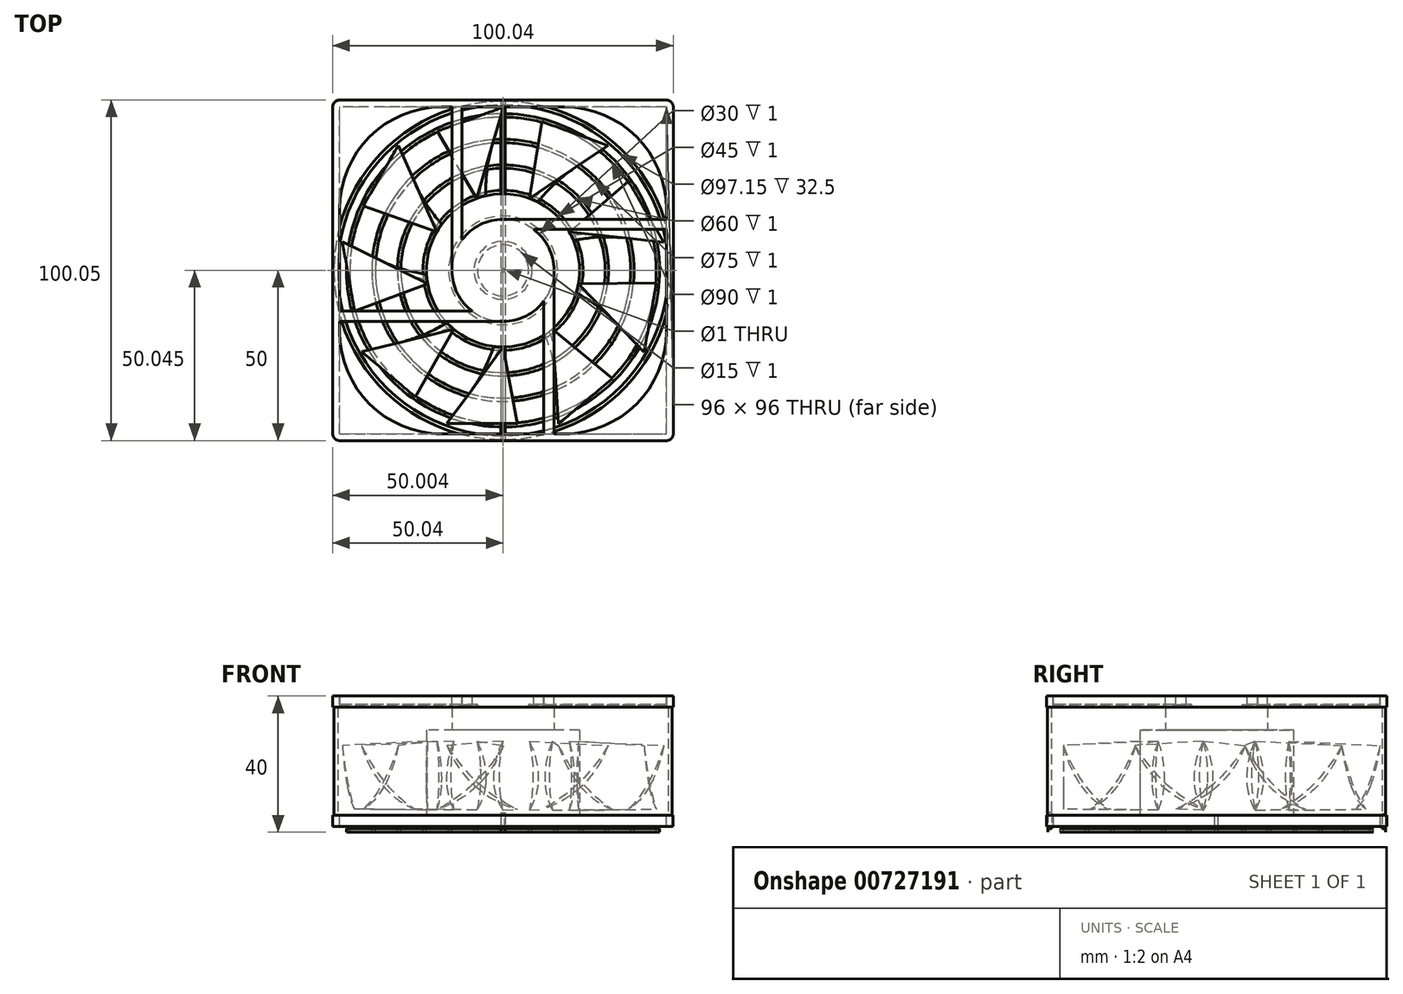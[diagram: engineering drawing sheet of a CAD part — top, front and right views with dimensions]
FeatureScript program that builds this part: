
annotation { "Feature Type Name" : "Feature", "Feature Type Description" : "" }
export const myFeature = defineFeature(function(context is Context, id is Id, definition is map)
    precondition{}
    {
        {
            var Q0;
            Q0=qCreatedBy(makeId("Top.planeOp"),FACE);
            var sketch = newSketch(context, id + "F0", { "sketchPlane" : qUnion([Q0])});
            skCircle(sketch, "E0", {"center": v(0, 0) * mm, "radius": 22.5 * mm});
            skSolve(sketch);
        }
        {
            var Q0;
            Q0=makeQuery(id+"F0.imprint","IMPRINT",FACE,{"disambiguationData":[TD([[makeQuery(id+"F0.imprint","IMPRINT",EDGE,{"derivedFrom":sQuery(id+"F0.wireOp",EDGE,"E0")}),1.0]])]});
            extrude(context, id + "F1", {"entities" : qUnion([Q0]), "depth" : 25 * mm, "offsetDistance" : 25 * mm});
        }
        {
            var Q0;
            Q0=qCreatedBy(makeId("Front.planeOp"),FACE);
            cPlane(context, id + "F2", {"entities" : qUnion([Q0]), "cplaneType" : CPlaneType.OFFSET, "offset" : 22.5 * mm, "width" : 150 * mm, "height" : 150 * mm});
        }
        {
            var Q0;
            Q0=qCreatedBy(id+"F2.planeOp",FACE);
            var sketch = newSketch(context, id + "F3", { "sketchPlane" : qUnion([Q0])});
            skArc(sketch, "E1", {"start": v(0, 21.74) * mm, "mid": v(-2.32, 15.5) * mm, "end": v(-2.7, 8.85) * mm});
            skArc(sketch, "E2", {"start": v(0, 21.74) * mm, "mid": v(-1.2, 11.6) * mm, "end": v(0, 1.47) * mm});
            skArc(sketch, "E3", {"start": v(-2.56, 14.16) * mm, "mid": v(-2.5, 7.57) * mm, "end": v(0, 1.47) * mm});
            skSolve(sketch);
        }
        {
            var Q0;
            Q0=qCreatedBy(id+"F2.planeOp",FACE);
            cPlane(context, id + "F4", {"entities" : qUnion([Q0]), "cplaneType" : CPlaneType.OFFSET, "offset" : 22.5 * mm, "width" : 150 * mm, "height" : 150 * mm});
        }
        {
            var Q0;
            Q0=qCreatedBy(id+"F4.planeOp",FACE);
            var sketch = newSketch(context, id + "F5", { "sketchPlane" : qUnion([Q0])});
            skArc(sketch, "E4", {"start": v(-16.45, 20.45) * mm, "mid": v(-8.34, 8.67) * mm, "end": v(4.18, 1.74) * mm});
            skArc(sketch, "E5", {"start": v(-16.45, 20.45) * mm, "mid": v(-7.5, 9.6) * mm, "end": v(4.18, 1.74) * mm});
            skSolve(sketch);
        }
        {
            var Q0;
            Q0=makeQuery(id+"F3.imprint","IMPRINT",FACE,{"disambiguationData":[TD([[makeQuery(id+"F3.imprint","IMPRINT",EDGE,{"derivedFrom":sQuery(id+"F3.wireOp",EDGE,"E1")}),1.0]])]});
            var Q1;
            Q1=makeQuery(id+"F5.imprint","IMPRINT",FACE,{"disambiguationData":[TD([[makeQuery(id+"F5.imprint","IMPRINT",EDGE,{"derivedFrom":sQuery(id+"F5.wireOp",EDGE,"E4")}),1.0]])]});
            loft(context, id + "F6", {"sheetProfilesArray" : [{ "sheetProfileEntities" : qUnion([Q0]) }, { "sheetProfileEntities" : qUnion([Q1]) }]});
        }
        {
            var Q0;
            {var subQ0=sQuery(id+"F3.wireOp",EDGE,"E2");Q0=makeQuery(id+"F6.opLoft","SWEPT_BODY",BODY,{"disambiguationData":[OSD([makeQuery(id+"F3.imprint","IMPRINT",FACE,{"disambiguationData":[TD([[makeQuery(id+"F3.imprint","IMPRINT",EDGE,{"derivedFrom":subQ0}),-1.0]])]}),makeQuery(id+"F5.imprint","IMPRINT",FACE,{"disambiguationData":[TD([[makeQuery(id+"F5.imprint","IMPRINT",EDGE,{"derivedFrom":sQuery(id+"F5.wireOp",EDGE,"E4")}),1.0]])]})])]});}
            var Q1;
            Q1=makeQuery(id+"F1.opExtrude","SWEPT_FACE",FACE,{"disambiguationData":[OSD([sQuery(id+"F0.wireOp",EDGE,"E0")])]});
            circularPattern(context, id + "F7", {"entities" : qUnion([Q0]), "axis" : qUnion([Q1]), "angle" : 360 * degree, "instanceCount" : 9, "equalSpace" : true});
        }
        {
            var Q0;
            Q0=makeQuery(id+"F1.opExtrude","CAP_FACE",FACE,{"disambiguationData":[OSD([sQuery(id+"F0.wireOp",EDGE,"E0")])],"isStart":false});
            var sketch = newSketch(context, id + "F8", { "sketchPlane" : qUnion([Q0])});
            skCircle(sketch, "E6", {"center": v(0, 0) * mm, "radius": 15 * mm});
            skSolve(sketch);
        }
        {
            var Q0;
            Q0 = qSketchRegion(id + "F8", true);
            extrude(context, id + "F9", {"entities" : qUnion([Q0]), "operationType" : NewBodyOperationType.ADD, "depth" : 10 * mm, "offsetDistance" : 25 * mm});
        }
        {
            var Q0;
            Q0=makeQuery(id+"F9.opExtrude","CAP_FACE",FACE,{"disambiguationData":[OSD([sQuery(id+"F8.wireOp",EDGE,"E6")])],"isStart":false});
            var sketch = newSketch(context, id + "F10", { "sketchPlane" : qUnion([Q0])});
            skLineSegment(sketch, "E7", {"start": v(-15, 0) * mm, "end": v(-15, 50) * mm});
            skLineSegment(sketch, "E8", {"start": v(0, 15) * mm, "end": v(50, 15) * mm});
            skLineSegment(sketch, "E9", {"start": v(15, 0) * mm, "end": v(15, -50) * mm});
            skLineSegment(sketch, "E10", {"start": v(0, -15) * mm, "end": v(-50, -15) * mm});
            skLineSegment(sketch, "E11", {"start": v(-15, 50) * mm, "end": v(-12, 50) * mm});
            skLineSegment(sketch, "E12", {"start": v(-12, 50) * mm, "end": v(-12, 9) * mm});
            skLineSegment(sketch, "E13", {"start": v(50, 15) * mm, "end": v(50, 12) * mm});
            skLineSegment(sketch, "E14", {"start": v(15, -50) * mm, "end": v(12, -50) * mm});
            skLineSegment(sketch, "E15", {"start": v(-50, -15) * mm, "end": v(-50, -12) * mm});
            skLineSegment(sketch, "E16", {"start": v(-50, -12) * mm, "end": v(-9, -12) * mm});
            skLineSegment(sketch, "E17", {"start": v(12, -50) * mm, "end": v(12, -9) * mm});
            skLineSegment(sketch, "E18", {"start": v(50, 12) * mm, "end": v(9, 12) * mm});
            skCircle(sketch, "E19", {"center": v(0, 0) * mm, "radius": 15 * mm});
            skSolve(sketch);
        }
        {
            var Q0;
            Q0 = qSketchRegion(id + "F10", true);
            extrude(context, id + "F11", {"entities" : qUnion([Q0]), "operationType" : NewBodyOperationType.ADD, "oppositeDirection" : true, "depth" : 3.3 * mm, "offsetDistance" : 25 * mm});
        }
        {
            var Q0;
            Q0=makeQuery(id+"F11.boolean.opBoolean","MERGE",FACE,{"derivedFrom":[makeQuery(id+"F9.opExtrude","CAP_FACE",FACE,{"disambiguationData":[OSD([sQuery(id+"F8.wireOp",EDGE,"E6")])],"isStart":false}),makeQuery(id+"F11.opExtrude","CAP_FACE",FACE,{"disambiguationData":[OSD([sQuery(id+"F10.wireOp",EDGE,"E7"),sQuery(id+"F10.wireOp",EDGE,"E8"),sQuery(id+"F10.wireOp",EDGE,"E9"),sQuery(id+"F10.wireOp",EDGE,"E10"),sQuery(id+"F10.wireOp",EDGE,"E11"),sQuery(id+"F10.wireOp",EDGE,"E12"),sQuery(id+"F10.wireOp",EDGE,"E13"),sQuery(id+"F10.wireOp",EDGE,"E14"),sQuery(id+"F10.wireOp",EDGE,"E15"),sQuery(id+"F10.wireOp",EDGE,"E16"),sQuery(id+"F10.wireOp",EDGE,"E17"),sQuery(id+"F10.wireOp",EDGE,"E18"),sQuery(id+"F10.wireOp",EDGE,"E19")])],"isStart":true})]});
            var sketch = newSketch(context, id + "F12", { "sketchPlane" : qUnion([Q0])});
            skLineSegment(sketch, "E20", {"start": v(-12, 50) * mm, "end": v(50, 50) * mm});
            skLineSegment(sketch, "E21", {"start": v(50, 50) * mm, "end": v(50, -50) * mm});
            skLineSegment(sketch, "E22", {"start": v(48, -50) * mm, "end": v(-50, -50) * mm});
            skLineSegment(sketch, "E23", {"start": v(-50, -50) * mm, "end": v(-50, 50) * mm});
            skLineSegment(sketch, "E24", {"start": v(-50, 50) * mm, "end": v(-12, 50) * mm});
            skLineSegment(sketch, "E25", {"start": v(-48, -48) * mm, "end": v(-48, 48) * mm});
            skLineSegment(sketch, "E26", {"start": v(48, 48) * mm, "end": v(-48, 48) * mm});
            skLineSegment(sketch, "E27", {"start": v(-48, -48) * mm, "end": v(48, -48) * mm});
            skLineSegment(sketch, "E28", {"start": v(48, -48) * mm, "end": v(48, 48) * mm});
            skPoint(sketch, "E29.end.orphan", {"position": v(48, -50) * mm});
            skLineSegment(sketch, "E30", {"start": v(48, -50) * mm, "end": v(50, -50) * mm});
            skSolve(sketch);
        }
        {
            var Q0;
            Q0 = qSketchRegion(id + "F12", true);
            extrude(context, id + "F13", {"entities" : qUnion([Q0]), "operationType" : NewBodyOperationType.ADD, "oppositeDirection" : true, "depth" : 3.3 * mm, "offsetDistance" : 25 * mm});
        }
        {
            var Q0;
            Q0=makeQuery(id+"F1.opExtrude","CAP_FACE",FACE,{"disambiguationData":[OSD([sQuery(id+"F0.wireOp",EDGE,"E0")])],"isStart":true});
            var sketch = newSketch(context, id + "F14", { "sketchPlane" : qUnion([Q0])});
            skCircle(sketch, "E31", {"center": v(0, 0) * mm, "radius": 48.58 * mm});
            skCircle(sketch, "E32", {"center": v(0, 0) * mm, "radius": 49.67 * mm});
            skSolve(sketch);
        }
        {
            var Q0;
            Q0=makeQuery(id+"F14.imprint","IMPRINT",FACE,{"disambiguationData":[TD([[makeQuery(id+"F14.imprint","IMPRINT",EDGE,{"derivedFrom":sQuery(id+"F14.wireOp",EDGE,"E31")}),-1.0]])]});
            extrude(context, id + "F15", {"entities" : qUnion([Q0]), "operationType" : NewBodyOperationType.ADD, "oppositeDirection" : true, "depth" : 32.5 * mm, "offsetDistance" : 25 * mm});
        }
        {
            var Q0;
            Q0=makeQuery(id+"F13.opExtrude","SWEPT_EDGE",EDGE,{"disambiguationData":[OSD([sQuery(id+"F12.wireOp",EDGE,"E22"),sQuery(id+"F12.wireOp",EDGE,"E23")])]});
            fillet(context, id + "F16", {"entities" : qUnion([Q0]), "radius" : 2 * mm, "tangentPropagation" : true, "allowEdgeOverflow" : false});
        }
        {
            var Q0;
            Q0=makeQuery(id+"F13.opExtrude","SWEPT_EDGE",EDGE,{"disambiguationData":[OSD([sQuery(id+"F12.wireOp",EDGE,"E20"),sQuery(id+"F12.wireOp",EDGE,"E21")])]});
            var Q1;
            Q1=makeQuery(id+"F13.opExtrude","SWEPT_EDGE",EDGE,{"disambiguationData":[OSD([sQuery(id+"F12.wireOp",EDGE,"E23"),sQuery(id+"F12.wireOp",EDGE,"E24")])]});
            var Q2;
            Q2=makeQuery(id+"F13.opExtrude","SWEPT_EDGE",EDGE,{"disambiguationData":[OSD([sQuery(id+"F12.wireOp",EDGE,"E21"),sQuery(id+"F12.wireOp",EDGE,"E30")])]});
            fillet(context, id + "F17", {"entities" : qUnion([Q0, Q1, Q2]), "radius" : 2 * mm, "tangentPropagation" : true, "allowEdgeOverflow" : false});
        }
        {
            var Q0;
            Q0=makeQuery(id+"F1.opExtrude","CAP_FACE",FACE,{"disambiguationData":[OSD([sQuery(id+"F0.wireOp",EDGE,"E0")])],"isStart":true});
            var sketch = newSketch(context, id + "F18", { "sketchPlane" : qUnion([Q0])});
            skCircle(sketch, "E33", {"center": v(0, 0) * mm, "radius": 0.5 * mm});
            skSolve(sketch);
        }
        {
            var Q0;
            Q0=makeQuery(id+"F18.imprint","IMPRINT",FACE,{"disambiguationData":[TD([[makeQuery(id+"F18.imprint","IMPRINT",EDGE,{"derivedFrom":sQuery(id+"F18.wireOp",EDGE,"E33")}),1.0]])]});
            extrude(context, id + "F19", {"entities" : qUnion([Q0]), "operationType" : NewBodyOperationType.ADD, "depth" : 4 * mm, "offsetDistance" : 25 * mm});
        }
        {
            var Q0;
            Q0=makeQuery(id+"F19.opExtrude","CAP_FACE",FACE,{"disambiguationData":[OSD([sQuery(id+"F18.wireOp",EDGE,"E33")])],"isStart":false});
            var sketch = newSketch(context, id + "F20", { "sketchPlane" : qUnion([Q0])});
            skCircle(sketch, "E34", {"center": v(0, 0) * mm, "radius": 7.5 * mm});
            skCircle(sketch, "E35", {"center": v(0, 0) * mm, "radius": 8.5 * mm});
            skCircle(sketch, "E36", {"center": v(0, 0) * mm, "radius": 15 * mm});
            skCircle(sketch, "E37", {"center": v(0, 0) * mm, "radius": 16 * mm});
            skCircle(sketch, "E38", {"center": v(0, 0) * mm, "radius": 22.5 * mm});
            skCircle(sketch, "E39", {"center": v(0, 0) * mm, "radius": 23.5 * mm});
            skCircle(sketch, "E40", {"center": v(0, 0) * mm, "radius": 30 * mm});
            skCircle(sketch, "E41", {"center": v(0, 0) * mm, "radius": 31 * mm});
            skCircle(sketch, "E42", {"center": v(0, 0) * mm, "radius": 37.5 * mm});
            skCircle(sketch, "E43", {"center": v(0, 0) * mm, "radius": 38.5 * mm});
            skCircle(sketch, "E44", {"center": v(0, 0) * mm, "radius": 45 * mm});
            skCircle(sketch, "E45", {"center": v(0, 0) * mm, "radius": 46 * mm});
            skSolve(sketch);
        }
        {
            var Q0;
            Q0=makeQuery(id+"F20.imprint","IMPRINT",FACE,{"disambiguationData":[TD([[makeQuery(id+"F20.imprint","IMPRINT",EDGE,{"derivedFrom":sQuery(id+"F20.wireOp",EDGE,"E34")}),-1.0]])]});
            var Q1;
            Q1=makeQuery(id+"F20.imprint","IMPRINT",FACE,{"disambiguationData":[TD([[makeQuery(id+"F20.imprint","IMPRINT",EDGE,{"derivedFrom":sQuery(id+"F20.wireOp",EDGE,"E36")}),-1.0]])]});
            var Q2;
            Q2=makeQuery(id+"F20.imprint","IMPRINT",FACE,{"disambiguationData":[TD([[makeQuery(id+"F20.imprint","IMPRINT",EDGE,{"derivedFrom":sQuery(id+"F20.wireOp",EDGE,"E38")}),-1.0]])]});
            var Q3;
            Q3=makeQuery(id+"F20.imprint","IMPRINT",FACE,{"disambiguationData":[TD([[makeQuery(id+"F20.imprint","IMPRINT",EDGE,{"derivedFrom":sQuery(id+"F20.wireOp",EDGE,"E40")}),-1.0]])]});
            var Q4;
            Q4=makeQuery(id+"F20.imprint","IMPRINT",FACE,{"disambiguationData":[TD([[makeQuery(id+"F20.imprint","IMPRINT",EDGE,{"derivedFrom":sQuery(id+"F20.wireOp",EDGE,"E42")}),-1.0]])]});
            var Q5;
            Q5=makeQuery(id+"F20.imprint","IMPRINT",FACE,{"disambiguationData":[TD([[makeQuery(id+"F20.imprint","IMPRINT",EDGE,{"derivedFrom":sQuery(id+"F20.wireOp",EDGE,"E44")}),-1.0]])]});
            extrude(context, id + "F21", {"entities" : qUnion([Q0, Q1, Q2, Q3, Q4, Q5]), "depth" : 1 * mm, "offsetDistance" : 25 * mm});
        }
        {
            var Q0;
            Q0=makeQuery(id+"F19.opExtrude","CAP_FACE",FACE,{"disambiguationData":[OSD([sQuery(id+"F18.wireOp",EDGE,"E33")])],"isStart":false});
            var sketch = newSketch(context, id + "F22", { "sketchPlane" : qUnion([Q0])});
            skLineSegment(sketch, "E46.bottom", {"start": v(-0.66, -49.64) * mm, "end": v(0.66, -49.64) * mm});
            skLineSegment(sketch, "E46.top", {"start": v(-0.66, 49.64) * mm, "end": v(0.66, 49.64) * mm});
            skLineSegment(sketch, "E46.left", {"start": v(-0.66, -49.64) * mm, "end": v(-0.66, 49.64) * mm});
            skLineSegment(sketch, "E46.right", {"start": v(0.66, -49.64) * mm, "end": v(0.66, 49.64) * mm});
            skPoint(sketch, "E46.middle", {"position": v(0, 0) * mm});
            skSolve(sketch);
        }
        {
            var Q0;
            Q0=makeQuery(id+"F22.imprint","IMPRINT",FACE,{"disambiguationData":[TD([[makeQuery(id+"F22.imprint","IMPRINT",EDGE,{"derivedFrom":sQuery(id+"F22.wireOp",EDGE,"E46.bottom")}),1.0]])]});
            extrude(context, id + "F23", {"entities" : qUnion([Q0]), "depth" : 1 * mm, "offsetDistance" : 25 * mm});
        }
        {
            var Q0;
            Q0=makeQuery(id+"F23.opExtrude","CAP_FACE",FACE,{"disambiguationData":[OSD([sQuery(id+"F18.wireOp",EDGE,"E33"),sQuery(id+"F22.wireOp",EDGE,"E46.bottom"),sQuery(id+"F22.wireOp",EDGE,"E46.top"),sQuery(id+"F22.wireOp",EDGE,"E46.left"),sQuery(id+"F22.wireOp",EDGE,"E46.right")])],"isStart":true});
            var sketch = newSketch(context, id + "F24", { "sketchPlane" : qUnion([Q0])});
            skLineSegment(sketch, "E47.bottom", {"start": v(0.66, 49.64) * mm, "end": v(-0.66, 49.64) * mm});
            skLineSegment(sketch, "E47.top", {"start": v(0.66, 48.64) * mm, "end": v(-0.66, 48.64) * mm});
            skLineSegment(sketch, "E47.left", {"start": v(0.66, 49.64) * mm, "end": v(0.66, 48.64) * mm});
            skLineSegment(sketch, "E47.right", {"start": v(-0.66, 49.64) * mm, "end": v(-0.66, 48.64) * mm});
            skSolve(sketch);
        }
        {
            var Q0;
            Q0=makeQuery(id+"F24.imprint","IMPRINT",FACE,{"disambiguationData":[TD([[makeQuery(id+"F24.imprint","IMPRINT",EDGE,{"derivedFrom":sQuery(id+"F24.wireOp",EDGE,"E47.bottom")}),-1.0]])]});
            extrude(context, id + "F25", {"entities" : qUnion([Q0]), "depth" : 4.35 * mm, "offsetDistance" : 25 * mm});
        }
        {
            var Q0;
            Q0=makeQuery(id+"F23.opExtrude","CAP_FACE",FACE,{"disambiguationData":[OSD([sQuery(id+"F18.wireOp",EDGE,"E33"),sQuery(id+"F22.wireOp",EDGE,"E46.bottom"),sQuery(id+"F22.wireOp",EDGE,"E46.top"),sQuery(id+"F22.wireOp",EDGE,"E46.left"),sQuery(id+"F22.wireOp",EDGE,"E46.right")])],"isStart":true});
            var sketch = newSketch(context, id + "F26", { "sketchPlane" : qUnion([Q0])});
            skLineSegment(sketch, "E48.bottom", {"start": v(-0.66, -49.64) * mm, "end": v(0.66, -49.64) * mm});
            skLineSegment(sketch, "E48.top", {"start": v(-0.66, -48.46) * mm, "end": v(0.66, -48.46) * mm});
            skLineSegment(sketch, "E48.left", {"start": v(-0.66, -49.64) * mm, "end": v(-0.66, -48.46) * mm});
            skLineSegment(sketch, "E48.right", {"start": v(0.66, -49.64) * mm, "end": v(0.66, -48.46) * mm});
            skSolve(sketch);
        }
        {
            var Q0;
            Q0=makeQuery(id+"F26.imprint","IMPRINT",FACE,{"disambiguationData":[TD([[makeQuery(id+"F26.imprint","IMPRINT",EDGE,{"derivedFrom":sQuery(id+"F26.wireOp",EDGE,"E48.bottom")}),1.0]])]});
            extrude(context, id + "F27", {"entities" : qUnion([Q0]), "depth" : 4.8 * mm, "offsetDistance" : 25 * mm});
        }
        {
            var Q0;
            Q0=qCreatedBy(makeId("Top.planeOp"),FACE);
            var sketch = newSketch(context, id + "F28", { "sketchPlane" : qUnion([Q0])});
            skLineSegment(sketch, "E49", {"start": v(-12.04, 50.05) * mm, "end": v(49.96, 50.05) * mm});
            skLineSegment(sketch, "E50", {"start": v(49.96, 50.05) * mm, "end": v(49.96, -49.95) * mm});
            skLineSegment(sketch, "E51", {"start": v(47.96, -49.95) * mm, "end": v(-50.04, -49.95) * mm});
            skLineSegment(sketch, "E52", {"start": v(-50.04, -49.95) * mm, "end": v(-50.04, 50.05) * mm});
            skLineSegment(sketch, "E53", {"start": v(-50.04, 50.05) * mm, "end": v(-12.04, 50.05) * mm});
            skLineSegment(sketch, "E54", {"start": v(-48.04, -47.95) * mm, "end": v(-48.04, 48.05) * mm});
            skLineSegment(sketch, "E55", {"start": v(47.96, 48.05) * mm, "end": v(-48.04, 48.05) * mm});
            skLineSegment(sketch, "E56", {"start": v(-48.04, -47.95) * mm, "end": v(47.96, -47.95) * mm});
            skLineSegment(sketch, "E57", {"start": v(47.96, -47.95) * mm, "end": v(47.96, 48.05) * mm});
            skPoint(sketch, "E58.end.orphan", {"position": v(47.96, -49.95) * mm});
            skLineSegment(sketch, "E59", {"start": v(47.96, -49.95) * mm, "end": v(49.96, -49.95) * mm});
            skSolve(sketch);
        }
        {
            var Q0;
            Q0=makeQuery(id+"F28.imprint","IMPRINT",FACE,{"disambiguationData":[TD([[makeQuery(id+"F28.imprint","IMPRINT",EDGE,{"derivedFrom":sQuery(id+"F28.wireOp",EDGE,"E49")}),-1.0]])]});
            extrude(context, id + "F29", {"entities" : qUnion([Q0]), "oppositeDirection" : true, "depth" : 3.3 * mm, "offsetDistance" : 25 * mm});
        }
        {
            var Q0;
            Q0=makeQuery(id+"F29.opExtrude","SWEPT_EDGE",EDGE,{"disambiguationData":[OSD([sQuery(id+"F28.wireOp",EDGE,"E49"),sQuery(id+"F28.wireOp",EDGE,"E50")])]});
            var Q1;
            Q1=makeQuery(id+"F29.opExtrude","SWEPT_EDGE",EDGE,{"disambiguationData":[OSD([sQuery(id+"F28.wireOp",EDGE,"E52"),sQuery(id+"F28.wireOp",EDGE,"E53")])]});
            var Q2;
            Q2=makeQuery(id+"F29.opExtrude","SWEPT_EDGE",EDGE,{"disambiguationData":[OSD([sQuery(id+"F28.wireOp",EDGE,"E51"),sQuery(id+"F28.wireOp",EDGE,"E52")])]});
            var Q3;
            Q3=makeQuery(id+"F29.opExtrude","SWEPT_EDGE",EDGE,{"disambiguationData":[OSD([sQuery(id+"F28.wireOp",EDGE,"E50"),sQuery(id+"F28.wireOp",EDGE,"E59")])]});
            fillet(context, id + "F30", {"entities" : qUnion([Q0, Q1, Q2, Q3]), "radius" : 2 * mm, "tangentPropagation" : true, "allowEdgeOverflow" : false});
        }
        {
            var Q0;
            Q0=makeQuery(id+"F13.opExtrude","SWEPT_EDGE",EDGE,{"disambiguationData":[OSD([sQuery(id+"F12.wireOp",EDGE,"E25"),sQuery(id+"F12.wireOp",EDGE,"E26")])]});
            fillet(context, id + "F31", {"entities" : qUnion([Q0]), "radius" : 30 * mm, "tangentPropagation" : true, "allowEdgeOverflow" : false});
        }
        {
            var Q0;
            Q0=makeQuery(id+"F13.opExtrude","SWEPT_EDGE",EDGE,{"disambiguationData":[OSD([sQuery(id+"F12.wireOp",EDGE,"E26"),sQuery(id+"F12.wireOp",EDGE,"E28")])]});
            fillet(context, id + "F32", {"entities" : qUnion([Q0]), "radius" : 30 * mm, "tangentPropagation" : true, "allowEdgeOverflow" : false});
        }
        {
            var Q0;
            Q0=makeQuery(id+"F13.opExtrude","SWEPT_EDGE",EDGE,{"disambiguationData":[OSD([sQuery(id+"F12.wireOp",EDGE,"E27"),sQuery(id+"F12.wireOp",EDGE,"E28")])]});
            var Q1;
            Q1=makeQuery(id+"F13.opExtrude","SWEPT_EDGE",EDGE,{"disambiguationData":[OSD([sQuery(id+"F12.wireOp",EDGE,"E25"),sQuery(id+"F12.wireOp",EDGE,"E27")])]});
            fillet(context, id + "F33", {"entities" : qUnion([Q0, Q1]), "radius" : 30 * mm, "tangentPropagation" : true, "allowEdgeOverflow" : false});
        }
    });
